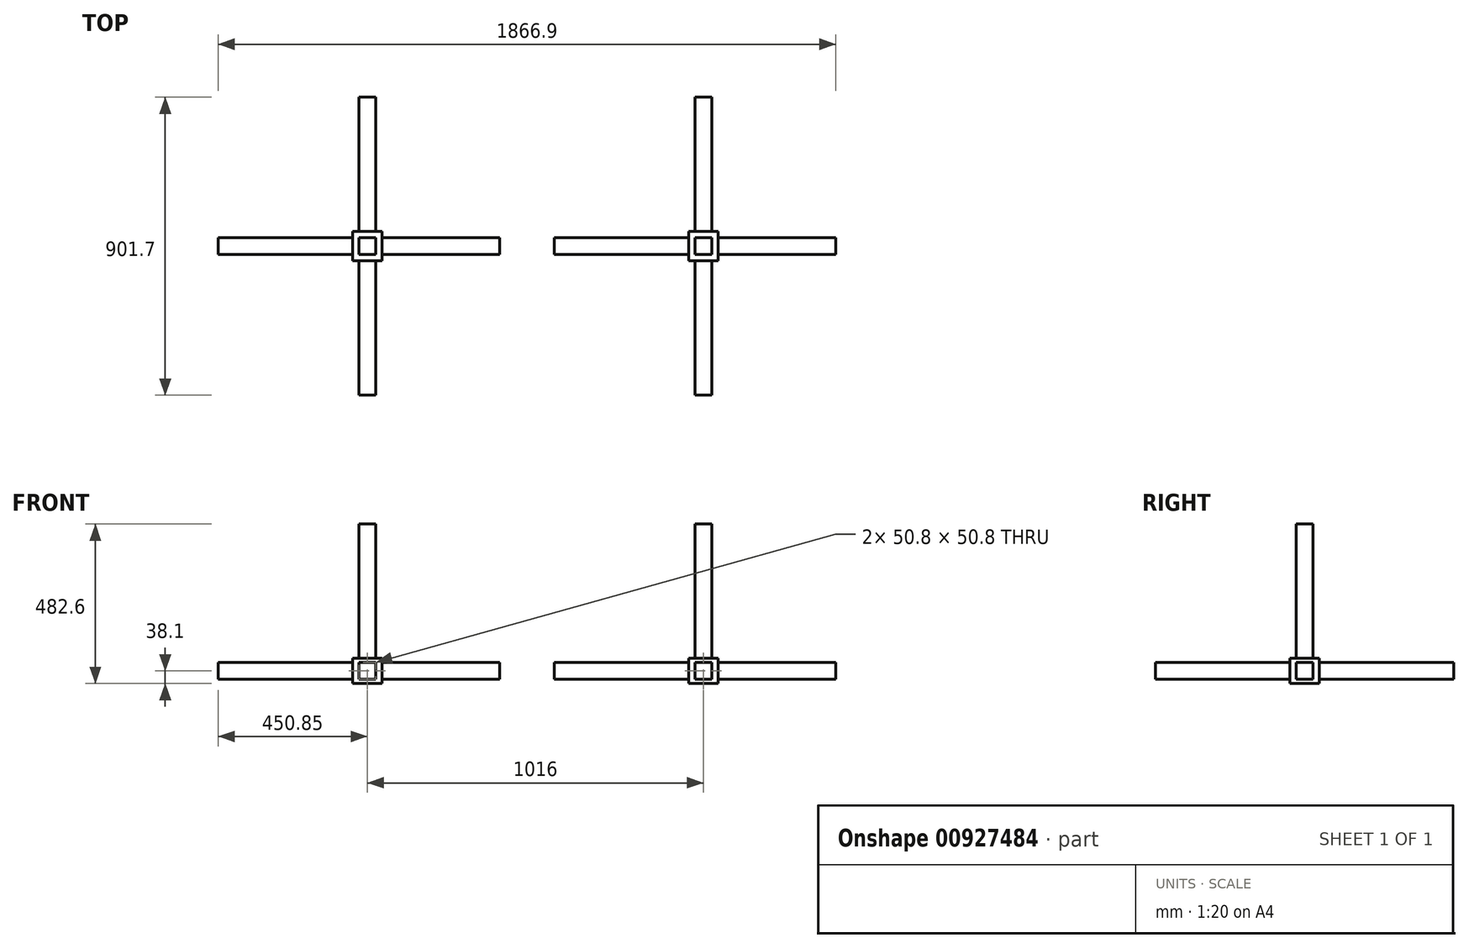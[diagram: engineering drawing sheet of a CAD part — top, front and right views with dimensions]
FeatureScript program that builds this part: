
annotation { "Feature Type Name" : "Feature", "Feature Type Description" : "" }
export const myFeature = defineFeature(function(context is Context, id is Id, definition is map)
    precondition{}
    {
        {
            var Q0;
            Q0=qCreatedBy(makeId("Top.planeOp"),FACE);
            var sketch = newSketch(context, id + "F0", { "sketchPlane" : qUnion([Q0])});
            skLineSegment(sketch, "E0.bottom", {"start": v(25.4, 25.4) * mm, "end": v(-25.4, 25.4) * mm});
            skLineSegment(sketch, "E0.top", {"start": v(25.4, -25.4) * mm, "end": v(-25.4, -25.4) * mm});
            skLineSegment(sketch, "E0.left", {"start": v(25.4, 25.4) * mm, "end": v(25.4, -25.4) * mm});
            skLineSegment(sketch, "E0.right", {"start": v(-25.4, 25.4) * mm, "end": v(-25.4, -25.4) * mm});
            skPoint(sketch, "E0.middle", {"position": v(0, 0) * mm});
            skSolve(sketch);
        }
        {
            var Q0;
            Q0=makeQuery(id+"F0.imprint","IMPRINT",FACE,{"disambiguationData":[TD([[makeQuery(id+"F0.imprint","IMPRINT",EDGE,{"derivedFrom":sQuery(id+"F0.wireOp",EDGE,"E0.bottom")}),1.0]])]});
            extrude(context, id + "F1", {"entities" : qUnion([Q0]), "depth" : 406.4 * mm, "offsetDistance" : 25.4 * mm});
        }
        {
            var Q0;
            Q0=qCreatedBy(makeId("Top.planeOp"),FACE);
            var sketch = newSketch(context, id + "F2", { "sketchPlane" : qUnion([Q0])});
            skLineSegment(sketch, "E1.bottom", {"start": v(-44.45, 44.45) * mm, "end": v(44.45, 44.45) * mm});
            skLineSegment(sketch, "E1.top", {"start": v(-44.45, -44.45) * mm, "end": v(44.45, -44.45) * mm});
            skLineSegment(sketch, "E1.left", {"start": v(-44.45, 44.45) * mm, "end": v(-44.45, -44.45) * mm});
            skLineSegment(sketch, "E1.right", {"start": v(44.45, 44.45) * mm, "end": v(44.45, -44.45) * mm});
            skPoint(sketch, "E1.middle", {"position": v(0, 0) * mm});
            skSolve(sketch);
        }
        {
            var Q0;
            Q0=makeQuery(id+"F2.imprint","IMPRINT",FACE,{"disambiguationData":[TD([[makeQuery(id+"F2.imprint","IMPRINT",EDGE,{"derivedFrom":sQuery(id+"F2.wireOp",EDGE,"E1.bottom")}),-1.0]])]});
            extrude(context, id + "F3", {"entities" : qUnion([Q0]), "operationType" : NewBodyOperationType.ADD, "oppositeDirection" : true, "depth" : 76.2 * mm, "offsetDistance" : 25.4 * mm});
        }
        {
            var Q0;
            Q0=makeQuery(id+"F3.opExtrude","SWEPT_FACE",FACE,{"disambiguationData":[OSD([sQuery(id+"F2.wireOp",EDGE,"E1.bottom")])]});
            var sketch = newSketch(context, id + "F4", { "sketchPlane" : qUnion([Q0])});
            skLineSegment(sketch, "E2.bottom", {"start": v(25.4, -63.5) * mm, "end": v(-25.4, -63.5) * mm});
            skLineSegment(sketch, "E2.top", {"start": v(25.4, -12.7) * mm, "end": v(-25.4, -12.7) * mm});
            skLineSegment(sketch, "E2.left", {"start": v(25.4, -63.5) * mm, "end": v(25.4, -12.7) * mm});
            skLineSegment(sketch, "E2.right", {"start": v(-25.4, -63.5) * mm, "end": v(-25.4, -12.7) * mm});
            skPoint(sketch, "E2.middle", {"position": v(0, -38.1) * mm});
            skPoint(sketch, "E2.middle.positionSnap0", {"position": v(44.45, -38.1) * mm});
            skPoint(sketch, "E2.middle.positionSnap1", {"position": v(0, -76.2) * mm});
            skPoint(sketch, "E2.centerSnap0", {"position": v(44.45, -38.1) * mm});
            skPoint(sketch, "E2.centerSnap1", {"position": v(0, -76.2) * mm});
            skSolve(sketch);
        }
        {
            var Q0;
            Q0=makeQuery(id+"F4.imprint","IMPRINT",FACE,{"disambiguationData":[TD([[makeQuery(id+"F4.imprint","IMPRINT",EDGE,{"derivedFrom":sQuery(id+"F4.wireOp",EDGE,"E2.bottom")}),-1.0]])]});
            extrude(context, id + "F5", {"entities" : qUnion([Q0]), "operationType" : NewBodyOperationType.ADD, "depth" : 406.4 * mm, "offsetDistance" : 25.4 * mm});
        }
        {
            var Q0;
            Q0=makeQuery(id+"F3.opExtrude","SWEPT_FACE",FACE,{"disambiguationData":[OSD([sQuery(id+"F2.wireOp",EDGE,"E1.left")])]});
            var sketch = newSketch(context, id + "F6", { "sketchPlane" : qUnion([Q0])});
            skLineSegment(sketch, "E3.bottom", {"start": v(-25.4, -12.7) * mm, "end": v(25.4, -12.7) * mm});
            skLineSegment(sketch, "E3.top", {"start": v(-25.4, -63.5) * mm, "end": v(25.4, -63.5) * mm});
            skLineSegment(sketch, "E3.left", {"start": v(-25.4, -12.7) * mm, "end": v(-25.4, -63.5) * mm});
            skLineSegment(sketch, "E3.right", {"start": v(25.4, -12.7) * mm, "end": v(25.4, -63.5) * mm});
            skPoint(sketch, "E3.middle", {"position": v(0, -38.1) * mm});
            skPoint(sketch, "E3.middle.positionSnap0", {"position": v(-44.45, -38.1) * mm});
            skPoint(sketch, "E3.centerSnap0", {"position": v(-44.45, -38.1) * mm});
            skSolve(sketch);
        }
        {
            var Q0;
            Q0=makeQuery(id+"F6.imprint","IMPRINT",FACE,{"disambiguationData":[TD([[makeQuery(id+"F6.imprint","IMPRINT",EDGE,{"derivedFrom":sQuery(id+"F6.wireOp",EDGE,"E3.bottom")}),-1.0]])]});
            extrude(context, id + "F7", {"entities" : qUnion([Q0]), "operationType" : NewBodyOperationType.ADD, "oppositeDirection" : true, "depth" : 444.5 * mm, "offsetDistance" : 25.4 * mm});
        }
        {
            var Q0;
            Q0=makeQuery(id+"F3.opExtrude","SWEPT_FACE",FACE,{"disambiguationData":[OSD([sQuery(id+"F2.wireOp",EDGE,"E1.top")])]});
            var sketch = newSketch(context, id + "F8", { "sketchPlane" : qUnion([Q0])});
            skLineSegment(sketch, "E4.bottom", {"start": v(-25.4, -12.7) * mm, "end": v(25.4, -12.7) * mm});
            skLineSegment(sketch, "E4.top", {"start": v(-25.4, -63.5) * mm, "end": v(25.4, -63.5) * mm});
            skLineSegment(sketch, "E4.left", {"start": v(-25.4, -12.7) * mm, "end": v(-25.4, -63.5) * mm});
            skLineSegment(sketch, "E4.right", {"start": v(25.4, -12.7) * mm, "end": v(25.4, -63.5) * mm});
            skPoint(sketch, "E4.middle", {"position": v(0, -38.1) * mm});
            skPoint(sketch, "E4.middle.positionSnap0", {"position": v(44.45, -38.1) * mm});
            skPoint(sketch, "E4.centerSnap0", {"position": v(44.45, -38.1) * mm});
            skSolve(sketch);
        }
        {
            var Q0;
            Q0=makeQuery(id+"F8.imprint","IMPRINT",FACE,{"disambiguationData":[TD([[makeQuery(id+"F8.imprint","IMPRINT",EDGE,{"derivedFrom":sQuery(id+"F8.wireOp",EDGE,"E4.bottom")}),-1.0]])]});
            extrude(context, id + "F9", {"entities" : qUnion([Q0]), "operationType" : NewBodyOperationType.ADD, "depth" : 406.4 * mm, "offsetDistance" : 25.4 * mm});
        }
        {
            var Q0;
            Q0=makeQuery(id+"F3.opExtrude","SWEPT_FACE",FACE,{"disambiguationData":[OSD([sQuery(id+"F2.wireOp",EDGE,"E1.left")])]});
            var sketch = newSketch(context, id + "F10", { "sketchPlane" : qUnion([Q0])});
            skLineSegment(sketch, "E5.bottom", {"start": v(25.4, -12.7) * mm, "end": v(-25.4, -12.7) * mm});
            skLineSegment(sketch, "E5.top", {"start": v(25.4, -63.5) * mm, "end": v(-25.4, -63.5) * mm});
            skLineSegment(sketch, "E5.left", {"start": v(25.4, -12.7) * mm, "end": v(25.4, -63.5) * mm});
            skLineSegment(sketch, "E5.right", {"start": v(-25.4, -12.7) * mm, "end": v(-25.4, -63.5) * mm});
            skPoint(sketch, "E5.middle", {"position": v(0, -38.1) * mm});
            skPoint(sketch, "E5.middle.positionSnap0", {"position": v(-44.45, -38.1) * mm});
            skPoint(sketch, "E5.centerSnap0", {"position": v(-44.45, -38.1) * mm});
            skSolve(sketch);
        }
        {
            var Q0;
            Q0=makeQuery(id+"F10.imprint","IMPRINT",FACE,{"disambiguationData":[TD([[makeQuery(id+"F10.imprint","IMPRINT",EDGE,{"derivedFrom":sQuery(id+"F10.wireOp",EDGE,"E5.bottom")}),1.0]])]});
            extrude(context, id + "F11", {"entities" : qUnion([Q0]), "operationType" : NewBodyOperationType.ADD, "depth" : 406.4 * mm, "offsetDistance" : 25.4 * mm});
        }
        {
            var Q0;
            Q0=makeQuery(id+"F1.opExtrude","SWEPT_BODY",BODY,{"disambiguationData":[OSD([sQuery(id+"F0.wireOp",EDGE,"E0.bottom"),sQuery(id+"F0.wireOp",EDGE,"E0.top"),sQuery(id+"F0.wireOp",EDGE,"E0.left"),sQuery(id+"F0.wireOp",EDGE,"E0.right")])]});
            transform(context, id + "F12", {"entities" : qUnion([Q0]), "transformType" : TransformType.TRANSLATION_3D, "dx" : 1016 * mm, "dy" : 0 * mm, "dz" : 0 * mm, "makeCopy" : true});
        }
    });
